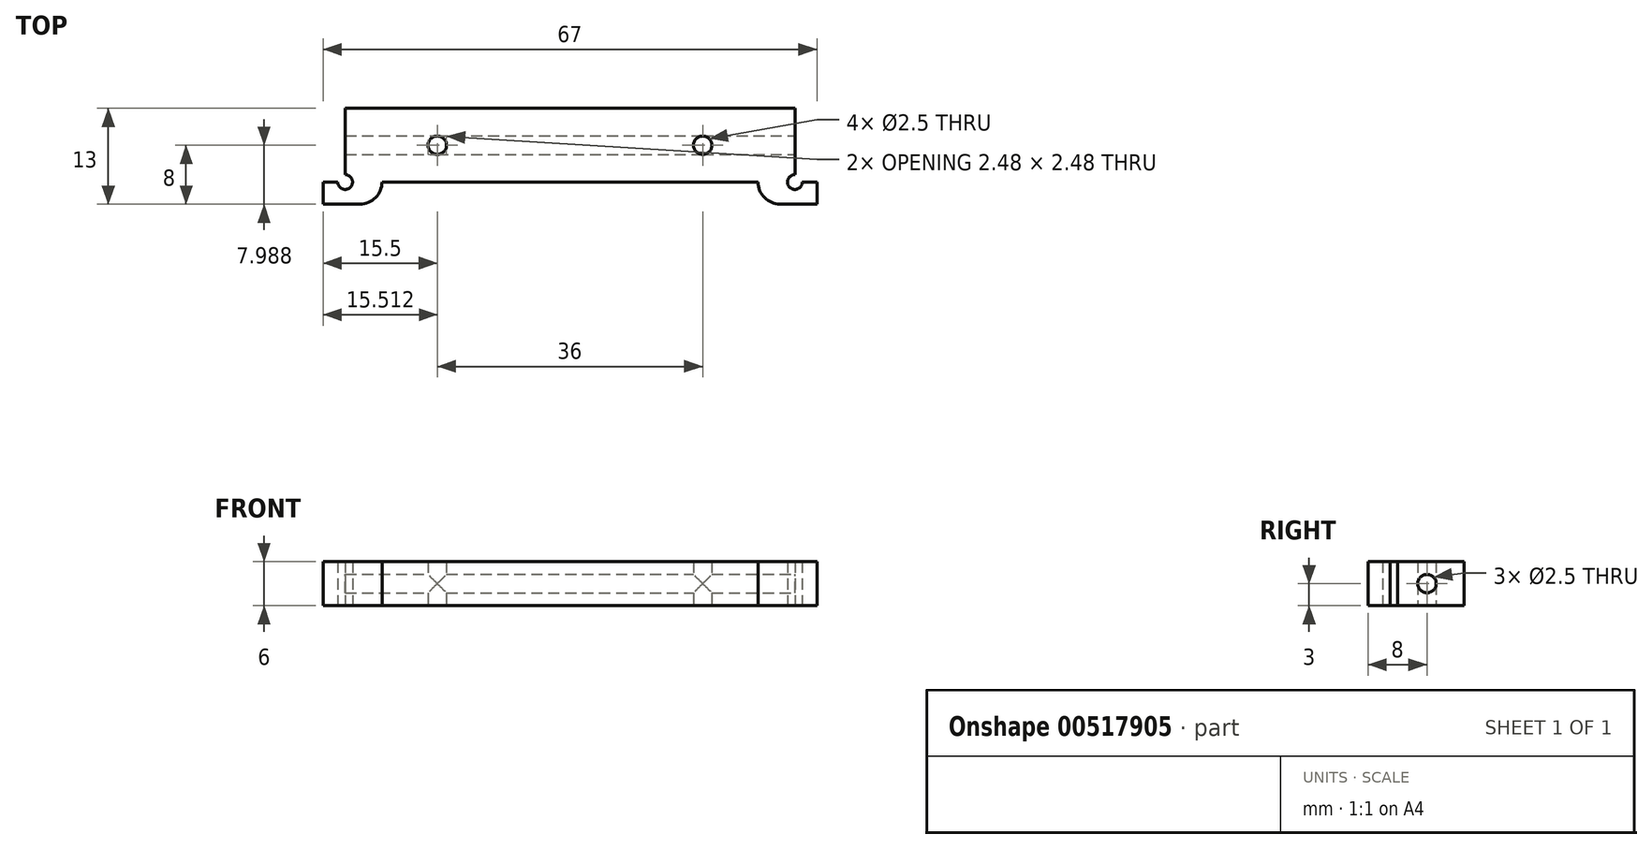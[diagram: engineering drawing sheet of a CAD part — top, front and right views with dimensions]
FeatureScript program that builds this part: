
annotation { "Feature Type Name" : "Feature", "Feature Type Description" : "" }
export const myFeature = defineFeature(function(context is Context, id is Id, definition is map)
    precondition{}
    {
        {
            var Q0;
            Q0=qCreatedBy(makeId("Top.planeOp"),FACE);
            var sketch = newSketch(context, id + "F0", { "sketchPlane" : qUnion([Q0])});
            skLineSegment(sketch, "E0.top", {"start": v(30.5, 5) * mm, "end": v(-30.5, 5) * mm});
            skLineSegment(sketch, "E0.left", {"start": v(30.5, -4) * mm, "end": v(30.5, 5) * mm});
            skLineSegment(sketch, "E0.right", {"start": v(-30.5, -4) * mm, "end": v(-30.5, 5) * mm});
            skPoint(sketch, "E0.middle", {"position": v(0, 0) * mm});
            skLineSegment(sketch, "E1", {"start": v(-33.5, -5) * mm, "end": v(-31.5, -5) * mm});
            skLineSegment(sketch, "E2", {"start": v(33.5, -5) * mm, "end": v(33.5, -8) * mm});
            skLineSegment(sketch, "E3", {"start": v(33.5, -8) * mm, "end": v(28.5, -8) * mm});
            skLineSegment(sketch, "E4", {"start": v(-33.5, -8) * mm, "end": v(-33.5, -5) * mm});
            skLineSegment(sketch, "E5.trimOffspring", {"start": v(31.5, -5) * mm, "end": v(33.5, -5) * mm});
            skLineSegment(sketch, "E6", {"start": v(25.5, -5) * mm, "end": v(25.5, -5) * mm});
            skLineSegment(sketch, "E7", {"start": v(-25.5, -5) * mm, "end": v(-25.5, -5) * mm});
            skLineSegment(sketch, "E8", {"start": v(25.5, -5) * mm, "end": v(-25.5, -5) * mm});
            skPoint(sketch, "E9.orphan", {"position": v(-25.5, -1.4) * mm});
            skPoint(sketch, "E10.orphan", {"position": v(25.5, -1.4) * mm});
            skLineSegment(sketch, "E11.trimOffspring", {"start": v(-28.5, -8) * mm, "end": v(-33.5, -8) * mm});
            skPoint(sketch, "E12.visualSharp", {"position": v(-25.5, -8) * mm});
            skArc(sketch, "E12.filletArc", {"start": v(-28.5, -8) * mm, "mid": v(-26.38, -7.12) * mm, "end": v(-25.5, -5) * mm});
            skPoint(sketch, "E13.visualSharp", {"position": v(25.5, -8) * mm});
            skArc(sketch, "E13.filletArc", {"start": v(25.5, -5) * mm, "mid": v(26.38, -7.12) * mm, "end": v(28.5, -8) * mm});
            skArc(sketch, "E14", {"start": v(30.5, -4) * mm, "mid": v(29.8, -5.7) * mm, "end": v(31.5, -5) * mm});
            skArc(sketch, "E15", {"start": v(-31.5, -5) * mm, "mid": v(-29.8, -5.7) * mm, "end": v(-30.5, -4) * mm});
            skCircle(sketch, "E16", {"center": v(18, 0) * mm, "radius": 1.25 * mm});
            skCircle(sketch, "E17.MirrorC", {"center": v(-18, 0) * mm, "radius": 1.25 * mm});
            skSolve(sketch);
        }
        {
            var Q0;
            Q0=makeQuery(id+"F0.imprint","IMPRINT",FACE,{"disambiguationData":[TD([[makeQuery(id+"F0.imprint","IMPRINT",EDGE,{"derivedFrom":sQuery(id+"F0.wireOp",EDGE,"E0.top")}),1.0]])]});
            extrude(context, id + "F1", {"entities" : qUnion([Q0]), "depth" : 6 * mm, "offsetDistance" : 25 * mm});
        }
        {
            var Q0;
            Q0=makeQuery(id+"F1.opExtrude","SWEPT_FACE",FACE,{"disambiguationData":[OSD([sQuery(id+"F0.wireOp",EDGE,"E0.left")])]});
            var sketch = newSketch(context, id + "F2", { "sketchPlane" : qUnion([Q0])});
            skCircle(sketch, "E18", {"center": v(0, 3) * mm, "radius": 1.25 * mm});
            skSolve(sketch);
        }
        {
            var Q0;
            Q0=makeQuery(id+"F2.imprint","IMPRINT",FACE,{"disambiguationData":[TD([[makeQuery(id+"F2.imprint","IMPRINT",EDGE,{"derivedFrom":sQuery(id+"F2.wireOp",EDGE,"E18")}),1.0]])]});
            extrude(context, id + "F3", {"entities" : qUnion([Q0]), "operationType" : NewBodyOperationType.REMOVE, "endBound" : BoundingType.THROUGH_ALL, "oppositeDirection" : true, "depth" : 25 * mm, "offsetDistance" : 25 * mm});
        }
    });
